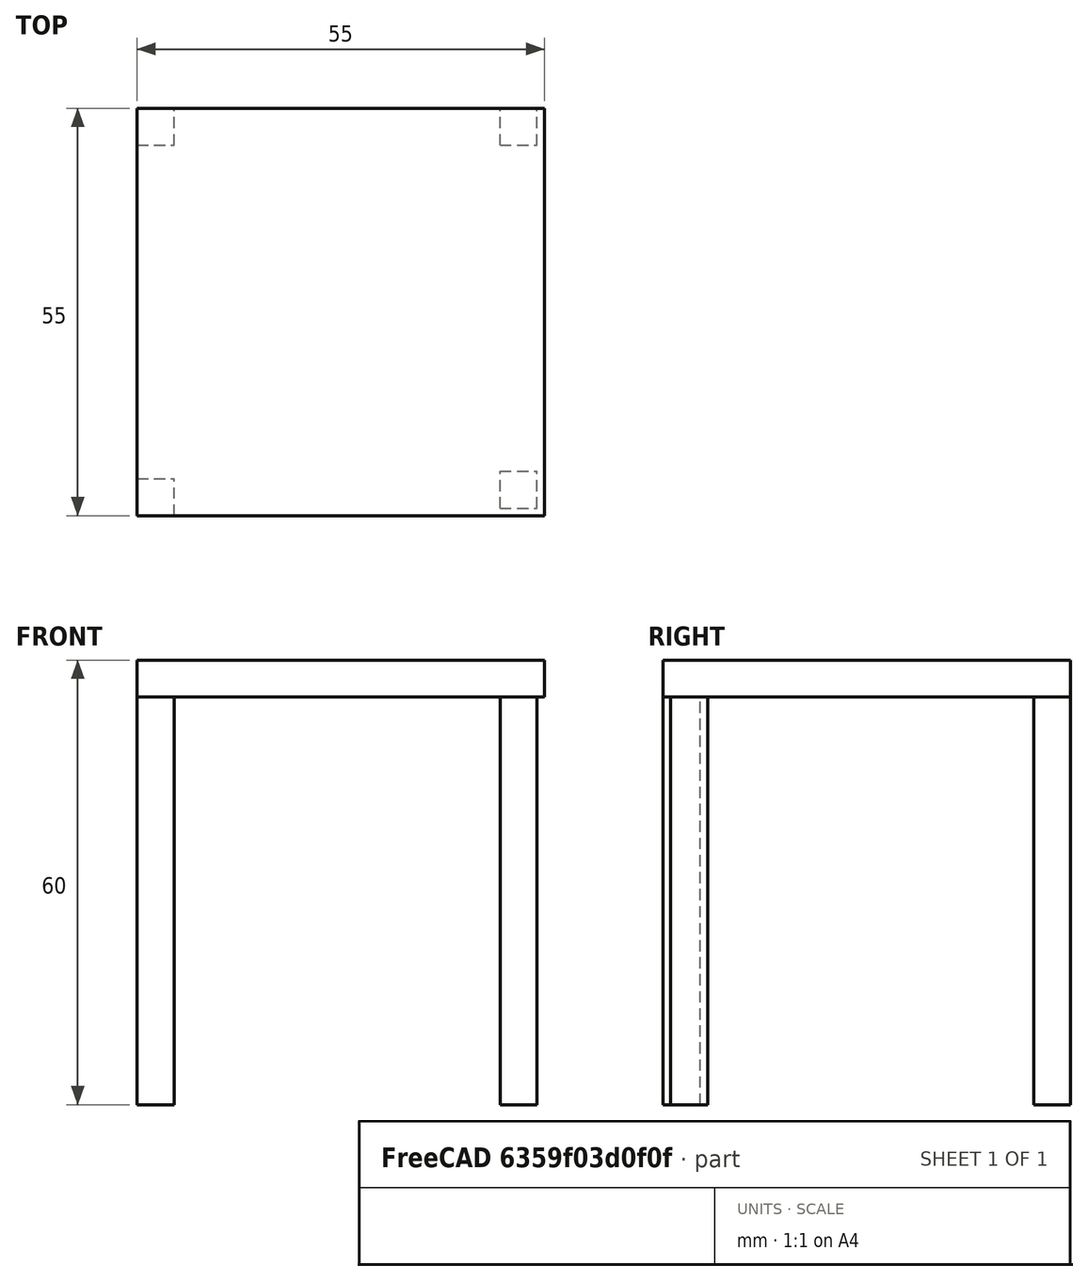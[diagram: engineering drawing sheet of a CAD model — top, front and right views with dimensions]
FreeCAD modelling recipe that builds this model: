
FCSTD DOCUMENT  (FreeCAD 0.19R)
Label: mesa_ikea
License: All rights reserved
LicenseURL: http://en.wikipedia.org/wiki/All_rights_reserved
objects: Part::Box×5
note: 5 computed .brp shape members not serialized (recipe doc carries the construction recipe); baked Part::Feature solids carry a one-line shape summary decoded from their .brp

FEATURE [Part::Box] Box001  label="Caja001"
  AttacherType = Attacher::AttachEngine3D
  Height = 5
  Length = 55
  Placement = pos=(0,0,37) rot=(0,0,1;0rad)
  Width = 55
FEATURE [Part::Box] Box002  label="Caja002"
  AttacherType = Attacher::AttachEngine3D
  Height = 55
  Length = 5
  Placement = pos=(0,0,-18) rot=(0,0,1;0rad)
  Width = 5
FEATURE [Part::Box] Box003  label="Caja003"
  AttacherType = Attacher::AttachEngine3D
  Height = 55
  Length = 5
  Placement = pos=(49,1,-18) rot=(0,0,1;0rad)
  Width = 5
FEATURE [Part::Box] Box004  label="Caja004"
  AttacherType = Attacher::AttachEngine3D
  Height = 55
  Length = 5
  Placement = pos=(49,50,-18) rot=(0,0,1;0rad)
  Width = 5
FEATURE [Part::Box] Box005  label="Caja005"
  AttacherType = Attacher::AttachEngine3D
  Height = 55
  Length = 5
  Placement = pos=(0,50,-18) rot=(0,0,1;0rad)
  Width = 5
